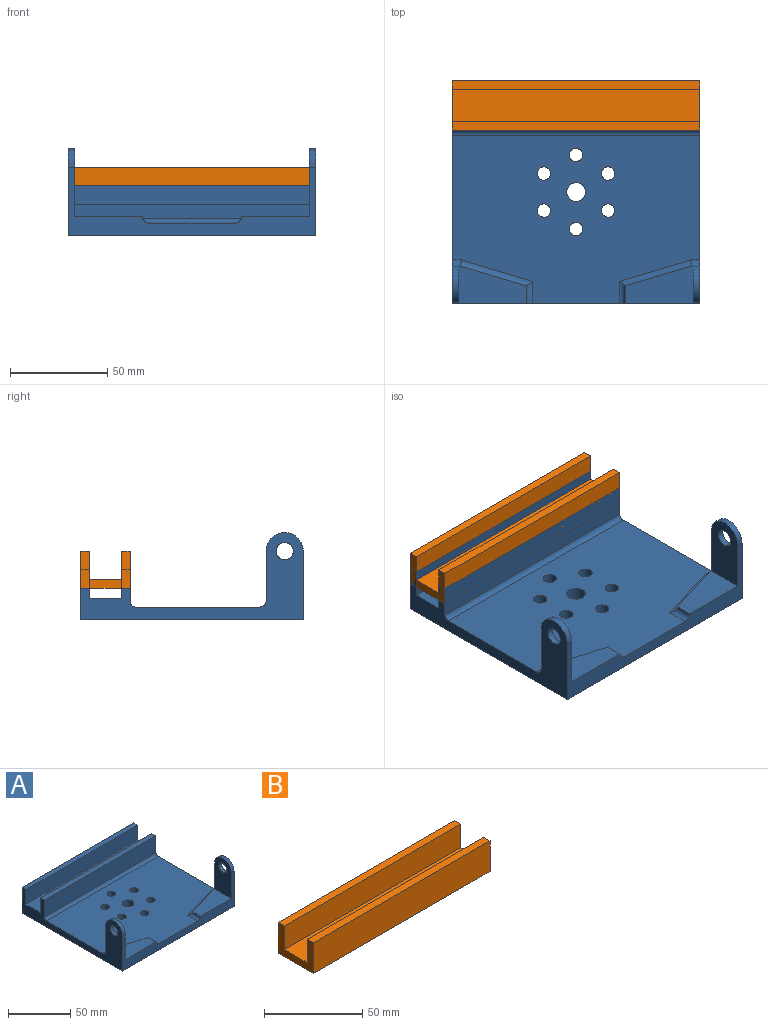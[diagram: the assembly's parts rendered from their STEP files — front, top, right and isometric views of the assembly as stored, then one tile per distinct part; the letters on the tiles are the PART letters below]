
ASSEMBLY  parts=2 mates=1
PART A: 36 faces, bbox 127x114.3x44.6 mm
  f0: plane 34.93x19.05mm, normal (0,0,1), area 492.7mm2, adj f5,f26,f33,f34,f35
  f1: plane 127x86.36mm, normal (0,0,1), area 9240.8mm2, adj f3,f4,f5,f7,f8,f9,f10,f11
  f2: plane 127x4.45mm, normal (0,0,1), area 564.5mm2, adj f3,f4,f6,f17
  f3: plane 114.3x44.58mm, normal (1,0,0), area 1599.3mm2, adj f1,f2,f5,f6,f14,f15,f16,f17
  f4: plane 114.3x44.58mm, normal (-1,0,0), area 1599.3mm2, adj f1,f2,f5,f6,f14,f15,f16,f17
  f5: plane 127x35.05mm, normal (0,-1,0), area 1214.8mm2, adj f0,f1,f3,f4,f14,f23,f24,f26
  f6: plane 127x25.4mm, normal (0,1,0), area 3225.8mm2, adj f2,f3,f4,f14
  f7: cylinder r=4.83mm len=9.65mm, axis (0,0,-1), area 192.5mm2, adj f1,f14
  f8: cylinder r=3.43mm len=6.86mm, axis (0,0,-1), area 136.8mm2, adj f1,f14
  f9: cylinder r=3.43mm len=6.86mm, axis (0,0,-1), area 136.8mm2, adj f1,f14
  f10: cylinder r=3.43mm len=6.86mm, axis (0,0,-1), area 136.8mm2, adj f1,f14
  f11: cylinder r=3.43mm len=6.86mm, axis (0,0,-1), area 136.8mm2, adj f1,f14
  f12: cylinder r=3.43mm len=6.86mm, axis (0,0,-1), area 136.8mm2, adj f1,f14
  f13: cylinder r=3.43mm len=6.86mm, axis (0,0,-1), area 136.8mm2, adj f1,f14
  f14: plane 127x114.3mm, normal (0,0,-1), area 14221.3mm2, adj f3,f4,f5,f6,f7,f8,f9,f10
  f15: plane 127x16.51mm, normal (0,-1,0), area 2096.8mm2, adj f3,f4,f16,f20
  f16: plane 127x4.45mm, normal (0,0,1), area 564.5mm2, adj f3,f4,f15,f18
  f17: plane 127x14.61mm, normal (0,-1,0), area 1854.8mm2, adj f2,f3,f4,f19
  f18: plane 127x14.61mm, normal (0,1,0), area 1854.8mm2, adj f3,f4,f16,f19
  f19: plane 127x16.51mm, normal (0,0,1), area 2096.8mm2, adj f3,f4,f17,f18
  f20: cylinder r=2.54mm len=127mm, axis (1,0,0), area 506.7mm2, adj f1,f3,f4,f15
  f21: plane 25.53x3.18mm, normal (0,1,0), area 81mm2, adj f4,f24,f26,f33
  f22: plane 25.53x3.18mm, normal (0,1,0), area 81mm2, adj f3,f27,f29,f30
  f23: plane 34.93x19.05mm, normal (0,0,1), area 492.7mm2, adj f5,f29,f30,f31,f32
  f24: cylinder r=9.53mm len=19.05mm, axis (-1,0,0), area 95mm2, adj f4,f5,f21,f26
  f25: cylinder r=4.45mm len=8.89mm, axis (-1,0,0), area 88.7mm2, adj f4,f26
  f26: plane 35.05x19.05mm, normal (1,0,0), area 566.7mm2, adj f0,f5,f21,f24,f25
  f27: cylinder r=9.53mm len=19.05mm, axis (1,0,0), area 95mm2, adj f3,f5,f22,f29
  f28: cylinder r=4.45mm len=8.89mm, axis (1,0,0), area 88.7mm2, adj f3,f29
  f29: plane 35.05x19.05mm, normal (-1,0,0), area 566.7mm2, adj f5,f22,f23,f27,f28
  f30: cylinder r=3.17mm len=4.58mm, axis (-1,0,0), area 21.3mm2, adj f1,f3,f22,f23,f31
  f31: cylinder r=3.17mm len=37.61mm, axis (-0.96,-0.29,0), area 182.1mm2, adj f1,f23,f30,f32
  f32: cylinder r=3.17mm len=11.25mm, axis (0,-1,0), area 48.6mm2, adj f1,f5,f23,f31
  f33: cylinder r=3.17mm len=4.58mm, axis (-1,0,0), area 21.3mm2, adj f0,f1,f4,f21,f34
  f34: cylinder r=3.17mm len=37.61mm, axis (-0.96,0.29,0), area 182.1mm2, adj f0,f1,f33,f35
  f35: cylinder r=3.17mm len=11.25mm, axis (0,1,0), area 48.6mm2, adj f0,f1,f5,f34
PART B: 10 faces, bbox 127x25.4x19.1 mm
  f0: plane 127x4.45mm, normal (0,0,1), area 564.5mm2, adj f1,f7,f8,f9
  f1: plane 127x14.61mm, normal (0,-1,0), area 1854.8mm2, adj f0,f2,f8,f9
  f2: plane 127x16.51mm, normal (0,0,1), area 2096.8mm2, adj f1,f3,f8,f9
  f3: plane 127x14.61mm, normal (0,1,0), area 1854.8mm2, adj f2,f4,f8,f9
  f4: plane 127x4.45mm, normal (0,0,1), area 564.5mm2, adj f3,f5,f8,f9
  f5: plane 127x19.05mm, normal (0,-1,0), area 2419.3mm2, adj f4,f6,f8,f9
  f6: plane 127x25.4mm, normal (0,0,-1), area 3225.8mm2, adj f5,f7,f8,f9
  f7: plane 127x19.05mm, normal (0,1,0), area 2419.3mm2, adj f0,f6,f8,f9
  f8: plane 25.4x19.05mm, normal (1,0,0), area 242.7mm2, adj f0,f1,f2,f3,f4,f5,f6,f7
  f9: plane 25.4x19.05mm, normal (-1,0,0), area 242.7mm2, adj f0,f1,f2,f3,f4,f5,f6,f7
PLACE A t=(-1.32,-0.84,-6.15)mm
PLACE B t=(-1.32,43.61,9.73)mm
MATE fastened B.f7 <-> A.f6  axis (0,1,0) through (-1.32,56.31,19.25)mm
